# Revit family: CADS_AIRFLOWdev_AirTerminal_CondensationTrap
name_source: partatom
category: Duct Accessories
revit_build: Autodesk Revit 2015 (Build: 20160512_0715(x64)
units: mm (PartAtom-declared; Revit-internal decimal feet)

## types (2) — shared parameters
6MonthlyMaintenance = Visually inspect system, clean the fan and ducting if necessary
AirflowRateRange = 0-61
AssetType = Fixed
CEApproval = Yes
Color = Grey
Constituents = Grey
DurationUnit = Years
E = 37 mm  [stored 0.121391 ft]
Exclusions = Incorrect Use / Incorrect Installation / Installed by a non-accredited electrician. Customer abuse.
F = 40 mm  [stored 0.131234 ft]
FaceType = LOUVERED
FlowControlType = NONE
Grade = Virgin
HasIntegralControl = No
HasSoundAttenuator = No
HasThermalInsulation = No
ISO140001 = Yes
ISO90001 = Yes
IsExtendedWarranty = No
Manufacturer = Airflow Developments Ltd
ManufacturerAddress = Aidelle House
Lancaster Road
Cressex Business Park
High Wycombe
Bucks
HP123QP
ManufacturerTelephone = 01494 525252
ManufacturerWebsite = www.airflow.com
Material = Plastic
MountingType = SURFACE
NBSCode = 90-75-50/370 Air terminals;
PointOfContact = Airflow Developments Ltd
ProductionYear = 2017
ServiceLifeDuration = 10
ServiceLifeType = EXPECTEDSERVICELIFE
Shape = Round
TapDia = 40 mm  [stored 0.131234 ft]
Uniclass2015 = Pr_65_70_46_01
WarrantyContent = Replacement of part if faulty
WarrantyGuarantor = Airflow Developments Ltd
WarrantyPeriod = 2
zero-valued in all types: NumberOfSlots

## per-type parameters (varying)
| type | A | B | C | D | Description | Dia | GrossWeight | ModelLabel | ModelReference | NominalHeight | NominalLength | NominalWidth | ReplacementCost | ShippingWeight | Size |
| 100 | 117 mm  [stored 0.383858 ft] | 110 mm  [stored 0.360892 ft] | 83 mm  [stored 0.27231 ft] | 52 mm | 100mm condensation trap | 100 mm  [stored 0.328084 ft] | 0.02 kg | 100mm condensation trap | 51978301 | 82 mm  [stored 0.269029 ft] | 100 mm  [stored 0.328084 ft] | 100 mm  [stored 0.328084 ft] | 25.44 | 0.02 kg | 100 x 100 x 82 |
| 150 | 168 mm  [stored 0.551181 ft] | 160 mm  [stored 0.524934 ft] | 112 mm  [stored 0.367454 ft] | 70 mm  [stored 0.229659 ft] | 150mm condensation trap | 150 mm | 0.03 kg | 150mm condensation trap | 52364801 | 112 mm  [stored 0.367454 ft] | 150 mm | 150 mm | 39.756 | 0.03 kg | 150 x 150 x 112 |

note: [stored X ft] marks values corroborated as IEEE doubles in the binary element streams (Revit-internal decimal feet)

## geometry (parser evidence)
native form markers: Blend x4, Sweep x1
no freeform markers — native parametric forms only
